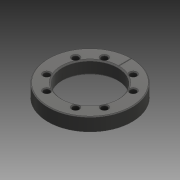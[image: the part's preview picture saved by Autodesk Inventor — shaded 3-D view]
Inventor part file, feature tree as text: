
AUTODESK INVENTOR PART (.ipt)
format: ipt  version: 2023 (Build 270158000, 158)  size: 202,240 bytes
history: native  units: mm
features: other x1, extrude x1, sketch x1, imported_body x1
ambient origin geometry x8: Origin, YZ Plane, XZ Plane, XY Plane, X Axis, Y Axis, Z Axis, Center Point
bodies: Body1 (feature_tree)
feature tree (4):
  other  "ソリッド1"
  extrude  "押し出し1"  TaperAngle=0.0deg  [1 undecoded]
  sketch  "スケッチ1"
  imported_body  "Base1"
note: 1 required parameter value undecoded (feature->parameter linkage not recoverable at this tier; creation-order binding heuristic only, values carry confidence <= 0.55)
